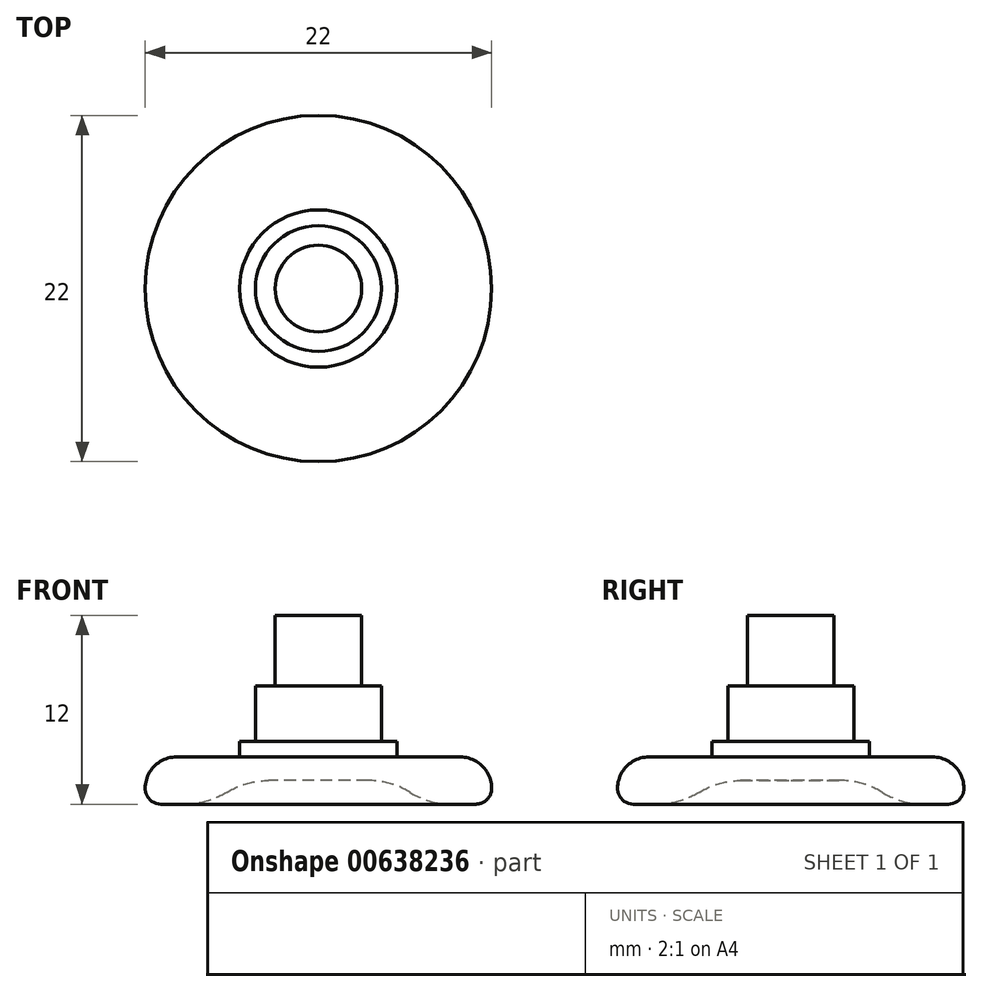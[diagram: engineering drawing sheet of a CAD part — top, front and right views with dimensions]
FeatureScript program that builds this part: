
annotation { "Feature Type Name" : "Feature", "Feature Type Description" : "" }
export const myFeature = defineFeature(function(context is Context, id is Id, definition is map)
    precondition{}
    {
        {
            assignVariable(context, id + "F0", {"name" : "PlateThickness", "anyValue" : 3});
        }
        {
            var Q0;
            Q0=qCreatedBy(makeId("Top.planeOp"),FACE);
            var sketch = newSketch(context, id + "F1", { "sketchPlane" : qUnion([Q0])});
            skCircle(sketch, "E0", {"center": v(0, 0) * mm, "radius": 11 * mm});
            skCircle(sketch, "E1", {"center": v(0, 0) * mm, "radius": 2.75 * mm});
            skCircle(sketch, "E2", {"center": v(0, 0) * mm, "radius": 5 * mm});
            skCircle(sketch, "E3", {"center": v(0, 0) * mm, "radius": 4 * mm});
            skSolve(sketch);
        }
        {
            var Q0;
            Q0=makeQuery(id+"F1.imprint","IMPRINT",FACE,{"disambiguationData":[TD([[makeQuery(id+"F1.imprint","IMPRINT",EDGE,{"derivedFrom":sQuery(id+"F1.wireOp",EDGE,"E0")}),1.0]])]});
            var Q1;
            Q1=makeQuery(id+"F1.imprint","IMPRINT",FACE,{"disambiguationData":[TD([[makeQuery(id+"F1.imprint","IMPRINT",EDGE,{"derivedFrom":sQuery(id+"F1.wireOp",EDGE,"eSHOdHc0-WQbQ-iaRl-N4qy-GDKkVdP7ETnB")}),-1.0]])]});
            var Q2;
            Q2=makeQuery(id+"F1.imprint","IMPRINT",FACE,{"disambiguationData":[TD([[makeQuery(id+"F1.imprint","IMPRINT",EDGE,{"derivedFrom":sQuery(id+"F1.wireOp",EDGE,"E1")}),-1.0]])]});
            var Q3;
            Q3=makeQuery(id+"F1.imprint","IMPRINT",FACE,{"disambiguationData":[TD([[makeQuery(id+"F1.imprint","IMPRINT",EDGE,{"derivedFrom":sQuery(id+"F1.wireOp",EDGE,"E2")}),1.0]])]});
            extrude(context, id + "F2", {"entities" : qUnion([Q0, Q1, Q2, Q3]), "depth" : (getVariable(context, 'PlateThickness')) * mm, "offsetDistance" : 25 * mm});
        }
        {
            var Q0;
            Q0=makeQuery(id+"F1.imprint","IMPRINT",FACE,{"disambiguationData":[TD([[makeQuery(id+"F1.imprint","IMPRINT",EDGE,{"derivedFrom":sQuery(id+"F1.wireOp",EDGE,"E1")}),1.0]])]});
            extrude(context, id + "F3", {"entities" : qUnion([Q0]), "operationType" : NewBodyOperationType.ADD, "depth" : (getVariable(context, 'PlateThickness') + 9) * mm, "offsetDistance" : 25 * mm, "hasSecondDirection" : true, "secondDirectionOppositeDirection" : false, "secondDirectionDepth" : 1.5 * mm});
        }
        {
            var Q0;
            Q0=makeQuery(id+"F1.imprint","IMPRINT",FACE,{"disambiguationData":[TD([[makeQuery(id+"F1.imprint","IMPRINT",EDGE,{"derivedFrom":sQuery(id+"F1.wireOp",EDGE,"E1")}),-1.0]])]});
            var Q1;
            Q1=makeQuery(id+"F1.imprint","IMPRINT",FACE,{"disambiguationData":[TD([[makeQuery(id+"F1.imprint","IMPRINT",EDGE,{"derivedFrom":sQuery(id+"F1.wireOp",EDGE,"E2")}),1.0]])]});
            var Q2;
            Q2=makeQuery(id+"F2.opExtrude","CAP_FACE",FACE,{"disambiguationData":[OSD([sQuery(id+"F1.wireOp",EDGE,"E0"),sQuery(id+"F1.wireOp",EDGE,"eSHOdHc0-WQbQ-iaRl-N4qy-GDKkVdP7ETnB")])],"isStart":false});
            extrude(context, id + "F4", {"entities" : qUnion([Q0, Q1]), "operationType" : NewBodyOperationType.ADD, "depth" : (getVariable(context, 'PlateThickness') + 1) * mm, "offsetDistance" : 25 * mm, "hasSecondDirection" : true, "secondDirectionBound" : SecondDirectionBoundingType.UP_TO_SURFACE, "secondDirectionOppositeDirection" : false, "secondDirectionDepth" : 25 * mm, "secondDirectionBoundEntityFace" : qUnion([Q2])});
        }
        {
            var Q0;
            Q0=makeQuery(id+"F1.imprint","IMPRINT",FACE,{"disambiguationData":[TD([[makeQuery(id+"F1.imprint","IMPRINT",EDGE,{"derivedFrom":sQuery(id+"F1.wireOp",EDGE,"E1")}),-1.0]])]});
            extrude(context, id + "F5", {"entities" : qUnion([Q0]), "operationType" : NewBodyOperationType.ADD, "depth" : (getVariable(context, 'PlateThickness') + 4.5) * mm, "offsetDistance" : 25 * mm});
        }
        {
            var Q0;
            Q0=makeQuery(id+"F2.opExtrude","CAP_EDGE",EDGE,{"disambiguationData":[OSD([sQuery(id+"F1.wireOp",EDGE,"E0")])],"isStart":true});
            fillet(context, id + "F6", {"entities" : qUnion([Q0]), "radius" : 1 * mm, "tangentPropagation" : true, "allowEdgeOverflow" : false});
        }
        {
            var Q0;
            Q0=makeQuery(id+"F2.opExtrude","CAP_EDGE",EDGE,{"disambiguationData":[OSD([sQuery(id+"F1.wireOp",EDGE,"E1")])],"isStart":true});
            chamfer(context, id + "F7", {"entities" : qUnion([Q0]), "width" : 4 * mm, "tangentPropagation" : true});
        }
        {
            var Q0;
            {var subQ0=sQuery(id+"F1.wireOp",EDGE,"E1");Q0=makeQuery(id+"F7.opChamfer","BLEND_EDGE",EDGE,{"blendedFrom":[makeQuery(id+"F2.opExtrude","CAP_EDGE",EDGE,{"disambiguationData":[OSD([subQ0])],"isStart":true}),makeQuery(id+"F3.opExtrude","CAP_FACE",FACE,{"disambiguationData":[OSD([subQ0])],"isStart":true})],"blendedInto":[makeQuery(id+"F3.opExtrude","CAP_FACE",FACE,{"disambiguationData":[OSD([subQ0])],"isStart":true})]});}
            fillet(context, id + "F8", {"entities" : qUnion([Q0]), "radius" : 5 * mm, "tangentPropagation" : true, "allowEdgeOverflow" : false});
        }
        {
            var Q0;
            {var subQ0=sQuery(id+"F1.wireOp",EDGE,"E1");Q0=makeQuery(id+"F7.opChamfer","BLEND_EDGE",EDGE,{"blendedFrom":[makeQuery(id+"F2.opExtrude","CAP_EDGE",EDGE,{"disambiguationData":[OSD([subQ0])],"isStart":true}),makeQuery(id+"F2.opExtrude","CAP_FACE",FACE,{"disambiguationData":[OSD([sQuery(id+"F1.wireOp",EDGE,"E0"),subQ0])],"isStart":true})],"blendedInto":[makeQuery(id+"F2.opExtrude","CAP_FACE",FACE,{"disambiguationData":[OSD([sQuery(id+"F1.wireOp",EDGE,"E0"),subQ0])],"isStart":true})]});}
            fillet(context, id + "F9", {"entities" : qUnion([Q0]), "radius" : 5 * mm, "tangentPropagation" : true, "allowEdgeOverflow" : false});
        }
        {
            var Q0;
            Q0=makeQuery(id+"F2.opExtrude","CAP_EDGE",EDGE,{"disambiguationData":[OSD([sQuery(id+"F1.wireOp",EDGE,"E0")])],"isStart":false});
            fillet(context, id + "F10", {"entities" : qUnion([Q0]), "radius" : 2 * mm, "tangentPropagation" : true, "allowEdgeOverflow" : false});
        }
    });
